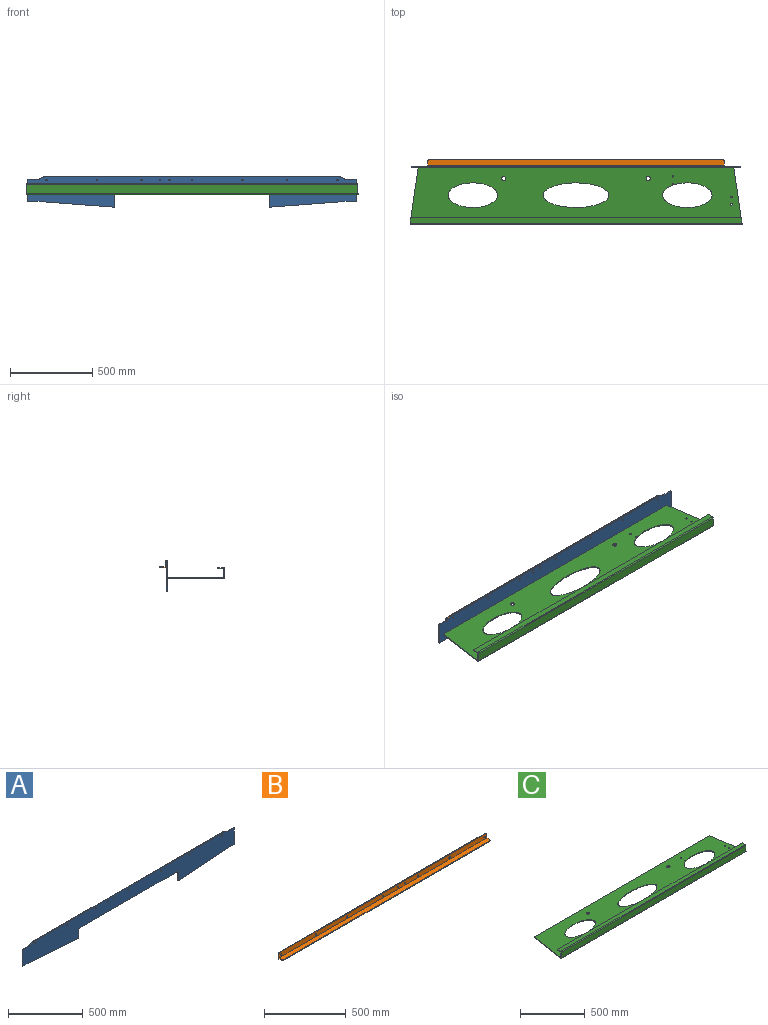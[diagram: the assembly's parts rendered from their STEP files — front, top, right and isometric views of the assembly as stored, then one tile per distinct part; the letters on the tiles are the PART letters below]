
ASSEMBLY  parts=3 mates=2
PART A: 29 faces, bbox 1996x6x185 mm
  f0: plane 1794.2x6mm, normal (0,0,1), area 10765.2mm2, adj f23,f24,f27,f28
  f1: plane 19.44x9.72mm, normal (-0.45,0,0.89), area 130.4mm2, adj f23,f24,f26,f27
  f2: plane 59.1x6mm, normal (0,0,1), area 354.6mm2, adj f3,f23,f24,f26
  f3: plane 135x6mm, normal (-1,0,0), area 810mm2, adj f2,f4,f23,f24
  f4: plane 61x6mm, normal (0,0,-1), area 366mm2, adj f3,f5,f23,f24
  f5: plane 467x35mm, normal (-0.07,0,-1), area 2809.9mm2, adj f4,f6,f23,f24
  f6: plane 80x6mm, normal (1,0,0), area 480mm2, adj f5,f7,f23,f24
  f7: plane 940x6mm, normal (0,0,-1), area 5640mm2, adj f6,f8,f23,f24
  f8: plane 80x6mm, normal (-1,0,0), area 480mm2, adj f7,f9,f23,f24
  f9: plane 467x35mm, normal (0.07,0,-1), area 2809.9mm2, adj f8,f10,f23,f24
  f10: plane 61x6mm, normal (0,0,-1), area 366mm2, adj f9,f11,f23,f24
  f11: plane 135x6mm, normal (1,0,0), area 810mm2, adj f10,f12,f23,f24
  f12: plane 59.1x6mm, normal (0,0,1), area 354.6mm2, adj f11,f23,f24,f25
  f13: cylinder r=5.5mm len=11mm, axis (0,-1,0), area 207.3mm2, adj f23,f24
  f14: cylinder r=5.5mm len=11mm, axis (0,-1,0), area 207.3mm2, adj f23,f24
  f15: cylinder r=5.5mm len=11mm, axis (0,-1,0), area 207.3mm2, adj f23,f24
  f16: cylinder r=5.5mm len=11mm, axis (0,-1,0), area 207.3mm2, adj f23,f24
  f17: cylinder r=5.5mm len=11mm, axis (0,-1,0), area 207.3mm2, adj f23,f24
  f18: cylinder r=5.5mm len=11mm, axis (0,-1,0), area 207.3mm2, adj f23,f24
  f19: cylinder r=5.5mm len=11mm, axis (0,-1,0), area 207.3mm2, adj f23,f24
  f20: cylinder r=5.5mm len=11mm, axis (0,-1,0), area 207.3mm2, adj f23,f24
  f21: cylinder r=5.5mm len=11mm, axis (0,-1,0), area 207.3mm2, adj f23,f24
  f22: plane 19.44x9.72mm, normal (0.45,0,0.89), area 130.4mm2, adj f23,f24,f25,f28
  f23: plane 1996x185mm, normal (0,-1,0), area 270189.7mm2, adj f0,f1,f2,f3,f4,f5,f6,f7
  f24: plane 1996x185mm, normal (0,1,0), area 270189.7mm2, adj f0,f1,f2,f3,f4,f5,f6,f7
  f25: cylinder r=25mm len=11.18mm, axis (0,1,0), area 69.5mm2, adj f12,f22,f23,f24
  f26: cylinder r=25mm len=11.18mm, axis (0,1,0), area 69.5mm2, adj f1,f2,f23,f24
  f27: cylinder r=25mm len=11.18mm, axis (0,1,0), area 69.5mm2, adj f0,f1,f23,f24
  f28: cylinder r=25mm len=11.18mm, axis (0,1,0), area 69.5mm2, adj f0,f22,f23,f24
PART B: 27 faces, bbox 1806x39x43 mm
  f0: plane 26.99x6mm, normal (1,0,0), area 161.9mm2, adj f12,f13,f14,f23
  f1: plane 1786x6mm, normal (0,0,1), area 10716mm2, adj f12,f13,f14,f15
  f2: cylinder r=5.5mm len=11mm, axis (0,-1,0), area 207.3mm2, adj f12,f13
  f3: cylinder r=5.5mm len=11mm, axis (0,-1,0), area 207.3mm2, adj f12,f13
  f4: cylinder r=5.5mm len=11mm, axis (0,-1,0), area 207.3mm2, adj f12,f13
  f5: cylinder r=5.5mm len=11mm, axis (0,-1,0), area 207.3mm2, adj f12,f13
  f6: cylinder r=5.5mm len=11mm, axis (0,-1,0), area 207.3mm2, adj f12,f13
  f7: cylinder r=5.5mm len=11mm, axis (0,-1,0), area 207.3mm2, adj f12,f13
  f8: cylinder r=5.5mm len=11mm, axis (0,-1,0), area 207.3mm2, adj f12,f13
  f9: cylinder r=5.5mm len=11mm, axis (0,-1,0), area 207.3mm2, adj f12,f13
  f10: cylinder r=5.5mm len=11mm, axis (0,-1,0), area 207.3mm2, adj f12,f13
  f11: plane 26.99x6mm, normal (-1,0,0), area 161.9mm2, adj f12,f13,f15,f24
  f12: plane 1806x36.99mm, normal (0,-1,0), area 65905.7mm2, adj f0,f1,f2,f3,f4,f5,f6,f7
  f13: plane 1806x36.99mm, normal (0,1,0), area 65905.7mm2, adj f0,f1,f2,f3,f4,f5,f6,f7
  f14: cylinder r=10mm len=10mm, axis (0,1,0), area 94.2mm2, adj f0,f1,f12,f13
  f15: cylinder r=10mm len=10mm, axis (0,-1,0), area 94.2mm2, adj f1,f11,f12,f13
  f16: plane 1786x6mm, normal (0,-1,0), area 10716mm2, adj f19,f20,f21,f22
  f17: plane 22.99x6mm, normal (1,0,0), area 137.9mm2, adj f19,f20,f22,f23
  f18: plane 22.99x6mm, normal (-1,0,0), area 137.9mm2, adj f19,f20,f21,f24
  f19: plane 1806x32.99mm, normal (0,0,1), area 59537mm2, adj f16,f17,f18,f21,f22,f26
  f20: plane 1806x32.99mm, normal (0,0,-1), area 59537mm2, adj f16,f17,f18,f21,f22,f25
  f21: cylinder r=10mm len=10mm, axis (0,0,1), area 94.2mm2, adj f16,f18,f19,f20
  f22: cylinder r=10mm len=10mm, axis (0,0,1), area 94.2mm2, adj f16,f17,f19,f20
  f23: plane 6.01x6.01mm, normal (1,0,0), area 28.4mm2, adj f0,f17,f25,f26
  f24: plane 6.01x6.01mm, normal (-1,0,0), area 28.4mm2, adj f11,f18,f25,f26
  f25: cylinder r=6.01mm len=1806mm, axis (1,0,0), area 17049.5mm2, adj f13,f20,f23,f24
  f26: cylinder r=0.01mm len=1806mm, axis (1,0,0), area 28.4mm2, adj f12,f19,f23,f24
PART C: 31 faces, bbox 2020x349x67 mm
  f0: plane 342.99x50mm, normal (0.99,0.14,0), area 2079.7mm2, adj f2,f12,f13,f27
  f1: plane 342.99x50mm, normal (-0.99,0.14,0), area 2079.7mm2, adj f2,f12,f13,f28
  f2: plane 1920x6mm, normal (0,1,0), area 11520mm2, adj f0,f1,f12,f13
  f3: cylinder r=5.5mm len=11mm, axis (0,0,-1), area 207.3mm2, adj f12,f13
  f4: cylinder r=5.5mm len=11mm, axis (0,0,-1), area 207.3mm2, adj f12,f13
  f5: cylinder r=4mm len=8mm, axis (0,0,-1), area 150.8mm2, adj f12,f13
  f6: cylinder r=4mm len=8mm, axis (0,0,-1), area 150.8mm2, adj f12,f13
  f7: cylinder r=12.5mm len=25mm, axis (0,0,-1), area 471.2mm2, adj f12,f13
  f8: cylinder r=12.5mm len=25mm, axis (0,0,-1), area 471.2mm2, adj f12,f13
  f9: extruded ~300x150mm, area 4359.9mm2, adj f12,f13
  f10: extruded ~300x150mm, area 4359.9mm2, adj f12,f13
  f11: extruded ~400x150mm, area 5456mm2, adj f12,f13
  f12: plane 2020x342.99mm, normal (0,0,-1), area 556608.3mm2, adj f0,f1,f2,f3,f4,f5,f6,f7
  f13: plane 2020x342.99mm, normal (0,0,1), area 556608.3mm2, adj f0,f1,f2,f3,f4,f5,f6,f7
  f14: plane 54.98x6mm, normal (-1,0,0), area 329.9mm2, adj f16,f17,f24,f28
  f15: plane 54.98x6mm, normal (1,0,0), area 329.9mm2, adj f16,f17,f23,f27
  f16: plane 2020x54.98mm, normal (0,-1,0), area 111059.6mm2, adj f14,f15,f25,f29
  f17: plane 2020x54.98mm, normal (0,1,0), area 111059.6mm2, adj f14,f15,f26,f30
  f18: plane 2020x6mm, normal (0,1,0), area 12120mm2, adj f19,f20,f21,f22
  f19: plane 34.99x6mm, normal (-1,0,0), area 209.9mm2, adj f18,f21,f22,f24
  f20: plane 34.99x6mm, normal (1,0,0), area 209.9mm2, adj f18,f21,f22,f23
  f21: plane 2020x34.99mm, normal (0,0,1), area 70679.8mm2, adj f18,f19,f20,f25
  f22: plane 2020x34.99mm, normal (0,0,-1), area 70679.8mm2, adj f18,f19,f20,f26
  f23: plane 6.01x6.01mm, normal (1,0,0), area 28.4mm2, adj f15,f20,f25,f26
  f24: plane 6.01x6.01mm, normal (-1,0,0), area 28.4mm2, adj f14,f19,f25,f26
  f25: cylinder r=6.01mm len=2020mm, axis (1,0,0), area 19069.8mm2, adj f16,f21,f23,f24
  f26: cylinder r=0.01mm len=2020mm, axis (1,0,0), area 31.7mm2, adj f17,f22,f23,f24
  f27: plane 6.01x6.01mm, normal (1,0,0), area 28.4mm2, adj f0,f15,f29,f30
  f28: plane 6.01x6.01mm, normal (-1,0,0), area 28.4mm2, adj f1,f14,f29,f30
  f29: cylinder r=6.01mm len=2020mm, axis (1,0,0), area 19069.8mm2, adj f12,f16,f27,f28
  f30: cylinder r=0.01mm len=2020mm, axis (1,0,0), area 31.7mm2, adj f13,f17,f27,f28
PLACE A t=(-626.95,214.56,-382.52)mm
PLACE B rot(axis=(0,0,1),180deg) t=(1276.05,214.56,-234.52)mm
PLACE C t=(-636.95,-134.44,-299.52)mm
MATE fastened B.f7 <-> A.f17  axis (0,1,0) through (65.55,220.56,-217.52)mm
MATE fastened A.f23 <-> C.f2  axis (0,-1,0) through (373.05,208.56,-302.52)mm
